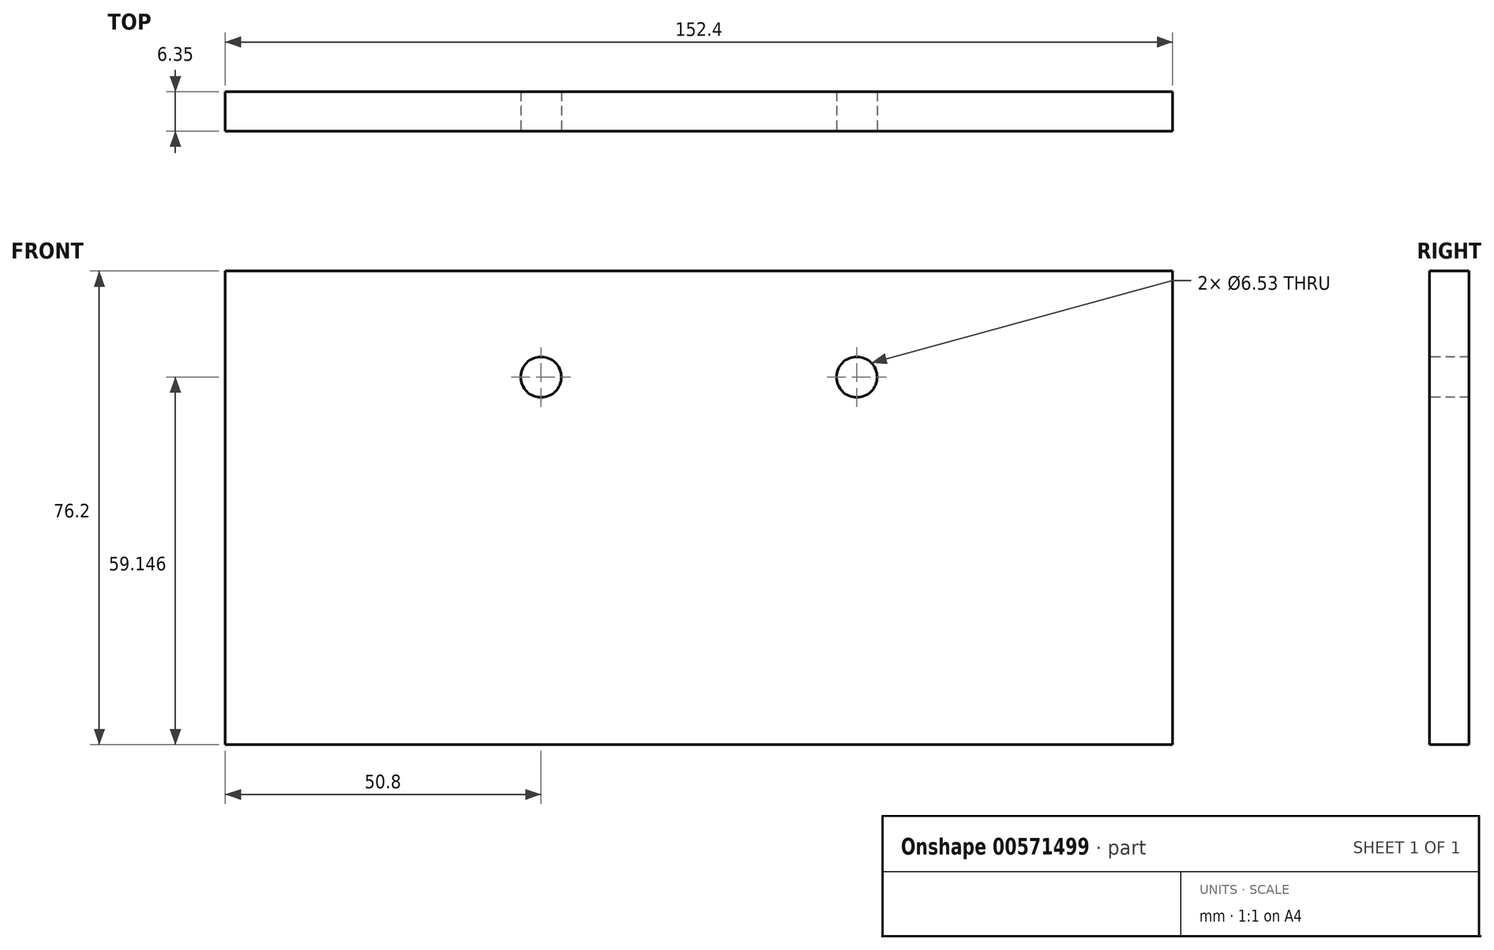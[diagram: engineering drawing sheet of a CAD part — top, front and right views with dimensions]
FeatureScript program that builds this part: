
annotation { "Feature Type Name" : "Feature", "Feature Type Description" : "" }
export const myFeature = defineFeature(function(context is Context, id is Id, definition is map)
    precondition{}
    {
        {
            var Q0;
            Q0=qCreatedBy(makeId("Top.planeOp"),FACE);
            var sketch = newSketch(context, id + "F0", { "sketchPlane" : qUnion([Q0])});
            skLineSegment(sketch, "E0.bottom", {"start": v(0, 55.12) * mm, "end": v(152.4, 55.12) * mm});
            skLineSegment(sketch, "E0.top", {"start": v(0, 48.77) * mm, "end": v(152.4, 48.77) * mm});
            skLineSegment(sketch, "E0.left", {"start": v(0, 55.12) * mm, "end": v(0, 48.77) * mm});
            skLineSegment(sketch, "E0.right", {"start": v(152.4, 55.12) * mm, "end": v(152.4, 48.77) * mm});
            skSolve(sketch);
        }
        {
            var Q0;
            Q0=makeQuery(id+"F0.imprint","IMPRINT",FACE,{"disambiguationData":[TD([[makeQuery(id+"F0.imprint","IMPRINT",EDGE,{"derivedFrom":sQuery(id+"F0.wireOp",EDGE,"E0.bottom")}),-1.0]])]});
            var Q1;
            Q1 = qSketchRegion(id + "F2", true);
            extrude(context, id + "F1", {"entities" : qUnion([Q0, Q1]), "depth" : 76.2 * mm, "offsetDistance" : 25.4 * mm});
        }
        {
            var Q0;
            Q0=makeQuery(id+"F1.opExtrude","SWEPT_FACE",FACE,{"disambiguationData":[OSD([sQuery(id+"F0.wireOp",EDGE,"E0.top")])]});
            var sketch = newSketch(context, id + "F2", { "sketchPlane" : qUnion([Q0])});
            skCircle(sketch, "E1", {"center": v(50.8, 59.15) * mm, "radius": 3.26 * mm});
            skCircle(sketch, "E2", {"center": v(101.6, 59.15) * mm, "radius": 3.26 * mm});
            skSolve(sketch);
        }
        {
            var Q0;
            Q0=makeQuery(id+"F2.imprint","IMPRINT",FACE,{"disambiguationData":[TD([[makeQuery(id+"F2.imprint","IMPRINT",EDGE,{"derivedFrom":sQuery(id+"F2.wireOp",EDGE,"E2")}),1.0]])]});
            var Q1;
            Q1=makeQuery(id+"F2.imprint","IMPRINT",FACE,{"disambiguationData":[TD([[makeQuery(id+"F2.imprint","IMPRINT",EDGE,{"derivedFrom":sQuery(id+"F2.wireOp",EDGE,"E1")}),1.0]])]});
            extrude(context, id + "F3", {"entities" : qUnion([Q0, Q1]), "operationType" : NewBodyOperationType.REMOVE, "endBound" : BoundingType.THROUGH_ALL, "oppositeDirection" : true, "depth" : 4.06 * mm, "offsetDistance" : 25.4 * mm});
        }
    });
